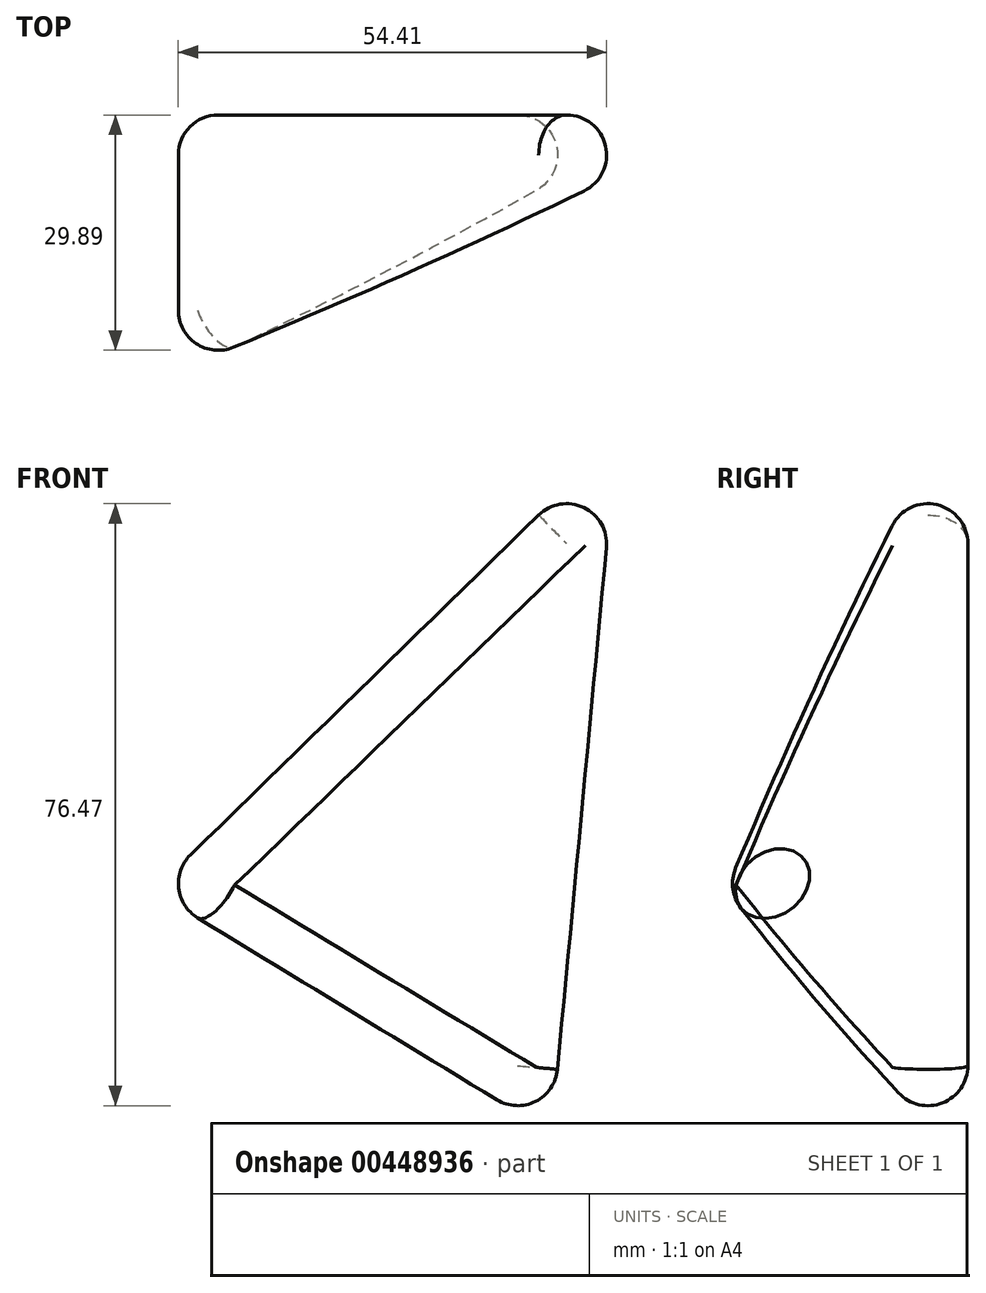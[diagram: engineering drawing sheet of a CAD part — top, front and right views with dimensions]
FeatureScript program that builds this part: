
annotation { "Feature Type Name" : "Feature", "Feature Type Description" : "" }
export const myFeature = defineFeature(function(context is Context, id is Id, definition is map)
    precondition{}
    {
        {
            var Q0;
            Q0=qCreatedBy(makeId("Front.planeOp"),FACE);
            var sketch = newSketch(context, id + "F0", { "sketchPlane" : qUnion([Q0])});
            skLineSegment(sketch, "E0", {"start": v(74.95, 73.16) * mm, "end": v(0, 0) * mm});
            skLineSegment(sketch, "E1", {"start": v(0, 0) * mm, "end": v(64.41, -39.18) * mm});
            skLineSegment(sketch, "E2", {"start": v(64.41, -39.18) * mm, "end": v(74.95, 73.16) * mm});
            skSolve(sketch);
        }
        {
            var Q0;
            Q0 = qSketchRegion(id + "F0", true);
            extrude(context, id + "F1", {"entities" : qUnion([Q0]), "depth" : 86.63 * mm});
        }
        {
            var Q0;
            Q0=makeQuery(id+"F1.opExtrude","CAP_EDGE",EDGE,{"disambiguationData":[OSD([sQuery(id+"F0.wireOp",EDGE,"E2")])],"isStart":false});
            fillet(context, id + "F2", {"entities" : qUnion([Q0]), "radius" : 655.96 * mm, "tangentPropagation" : true, "rho" : 0.5, "crossSection" : FilletCrossSection.CONIC, "allowEdgeOverflow" : false});
        }
        {
            var Q0;
            Q0=makeQuery(id+"F1.opExtrude","CAP_EDGE",EDGE,{"disambiguationData":[OSD([sQuery(id+"F0.wireOp",EDGE,"E0")])],"isStart":true});
            fillet(context, id + "F3", {"entities" : qUnion([Q0]), "radius" : 5.08 * mm, "tangentPropagation" : true, "allowEdgeOverflow" : false});
        }
        {
            var Q0;
            {var subQ0=sQuery(id+"F0.wireOp",EDGE,"E2");Q0=makeQuery(id+"F2.opFillet","BLEND_EDGE",EDGE,{"blendedFrom":[makeQuery(id+"F1.opExtrude","CAP_EDGE",EDGE,{"disambiguationData":[OSD([subQ0])],"isStart":false}),makeQuery(id+"F1.opExtrude","CAP_FACE",FACE,{"disambiguationData":[OSD([sQuery(id+"F0.wireOp",EDGE,"E0"),sQuery(id+"F0.wireOp",EDGE,"E1"),subQ0])],"isStart":true})],"blendedInto":[makeQuery(id+"F1.opExtrude","CAP_FACE",FACE,{"disambiguationData":[OSD([sQuery(id+"F0.wireOp",EDGE,"E0"),sQuery(id+"F0.wireOp",EDGE,"E1"),subQ0])],"isStart":true})]});}
            var Q1;
            Q1=makeQuery(id+"F2.opFillet","BLEND_EDGE",EDGE,{"blendedFrom":[makeQuery(id+"F1.opExtrude","CAP_EDGE",EDGE,{"disambiguationData":[OSD([sQuery(id+"F0.wireOp",EDGE,"E2")])],"isStart":false}),makeQuery(id+"F1.opExtrude","SWEPT_FACE",FACE,{"disambiguationData":[OSD([sQuery(id+"F0.wireOp",EDGE,"E0")])]})],"blendedInto":[makeQuery(id+"F1.opExtrude","SWEPT_FACE",FACE,{"disambiguationData":[OSD([sQuery(id+"F0.wireOp",EDGE,"E0")])]})]});
            var Q2;
            Q2=makeQuery(id+"F2.opFillet","BLEND_EDGE",EDGE,{"blendedFrom":[makeQuery(id+"F1.opExtrude","CAP_EDGE",EDGE,{"disambiguationData":[OSD([sQuery(id+"F0.wireOp",EDGE,"E2")])],"isStart":false}),makeQuery(id+"F1.opExtrude","SWEPT_FACE",FACE,{"disambiguationData":[OSD([sQuery(id+"F0.wireOp",EDGE,"E1")])]})],"blendedInto":[makeQuery(id+"F1.opExtrude","SWEPT_FACE",FACE,{"disambiguationData":[OSD([sQuery(id+"F0.wireOp",EDGE,"E1")])]})]});
            var Q3;
            Q3=makeQuery(id+"F1.opExtrude","CAP_EDGE",EDGE,{"disambiguationData":[OSD([sQuery(id+"F0.wireOp",EDGE,"E1")])],"isStart":true});
            fillet(context, id + "F4", {"entities" : qUnion([Q0, Q1, Q2, Q3]), "radius" : 5.08 * mm, "tangentPropagation" : true, "allowEdgeOverflow" : false});
        }
    });
